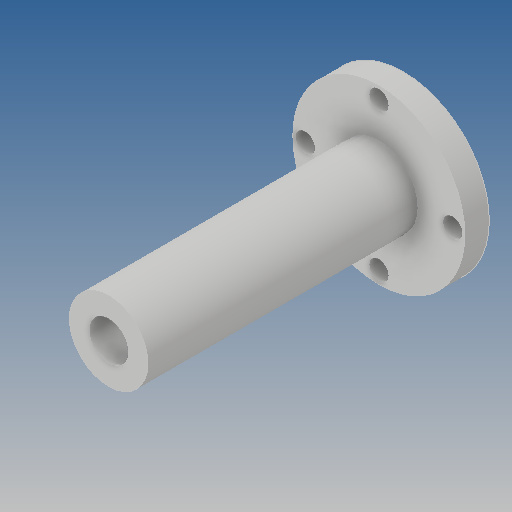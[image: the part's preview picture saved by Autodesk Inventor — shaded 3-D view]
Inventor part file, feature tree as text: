
AUTODESK INVENTOR PART (.ipt)
format: ipt  version: 2018 (Build 220112000, 112)  size: 140,288 bytes
history: native  units: mm
features: extrude x3, sketch x3, other x1
ambient origin geometry x8: Origin, YZ Plane, XZ Plane, XY Plane, X Axis, Y Axis, Z Axis, Center Point
bodies: Solid1 (feature_tree)
feature tree (7):
  other  "<userpath>\OneDrive\Objet3D\3DPrinter\Parameters.xlsx"
  extrude  "Extrusion1"  Depth=8.0mm
  extrude  "Extrusion2"  Depth=5.0mm
  extrude  "Extrusion3"  Depth=55.0mm
  sketch  "Sketch3"  dims[d0=8.0mm d1=35.0mm]
  sketch  "Sketch4"  dims[d2=5.0mm d3=0.0mm d4=16.0mm]
  sketch  "Sketch5"  dims[d5=8.0mm d6=55.0mm d7=0.0mm d8=4.0mm d9=15.0mm d10=15.0mm d11=15.0mm d12=15.0mm d13=4.0mm d14=4.0mm d15=4.0mm d16=55.0mm d17=0.0mm]
